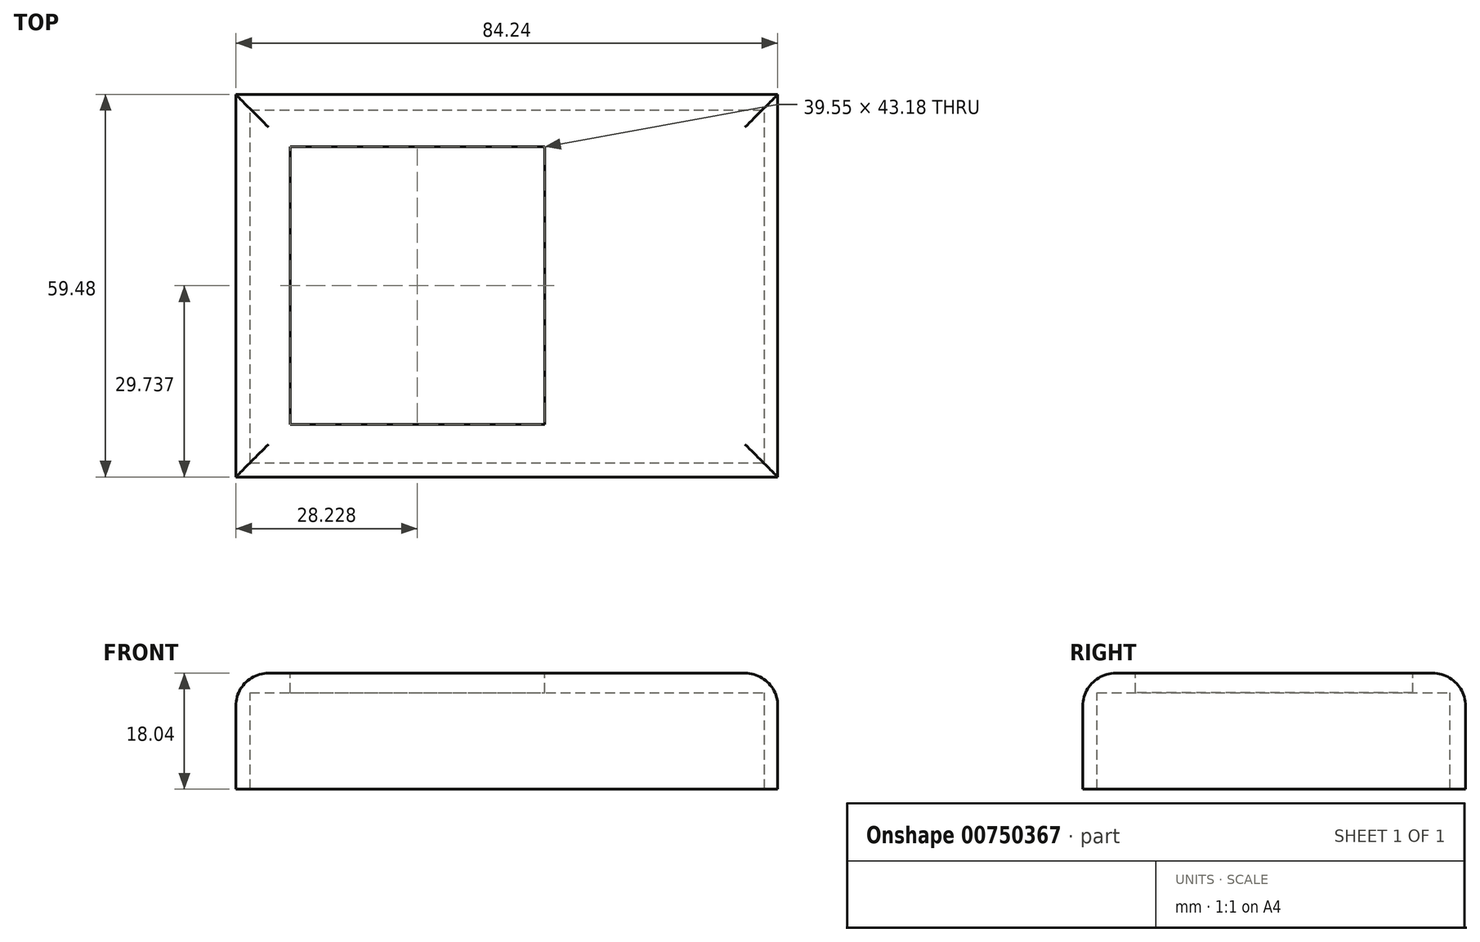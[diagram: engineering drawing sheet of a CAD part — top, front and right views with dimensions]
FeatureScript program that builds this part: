
annotation { "Feature Type Name" : "Feature", "Feature Type Description" : "" }
export const myFeature = defineFeature(function(context is Context, id is Id, definition is map)
    precondition{}
    {
        {
            var Q0;
            Q0=qCreatedBy(makeId("Top.planeOp"),FACE);
            var sketch = newSketch(context, id + "F0", { "sketchPlane" : qUnion([Q0])});
            skLineSegment(sketch, "E0.bottom", {"start": v(-43.4, 26.95) * mm, "end": v(40.84, 26.95) * mm});
            skLineSegment(sketch, "E0.top", {"start": v(-43.4, -32.53) * mm, "end": v(40.84, -32.53) * mm});
            skLineSegment(sketch, "E0.left", {"start": v(-43.4, 26.95) * mm, "end": v(-43.4, -32.53) * mm});
            skLineSegment(sketch, "E0.right", {"start": v(40.84, 26.95) * mm, "end": v(40.84, -32.53) * mm});
            skSolve(sketch);
        }
        {
            var Q0;
            Q0 = qSketchRegion(id + "F0", true);
            extrude(context, id + "F1", {"entities" : qUnion([Q0]), "depth" : 3.05 * mm, "offsetDistance" : 25.4 * mm});
        }
        {
            var Q0;
            Q0=makeQuery(id+"F1.opExtrude","CAP_FACE",FACE,{"disambiguationData":[OSD([sQuery(id+"F0.wireOp",EDGE,"E0.bottom"),sQuery(id+"F0.wireOp",EDGE,"E0.top"),sQuery(id+"F0.wireOp",EDGE,"E0.left"),sQuery(id+"F0.wireOp",EDGE,"E0.right")])],"isStart":true});
            var sketch = newSketch(context, id + "F2", { "sketchPlane" : qUnion([Q0])});
            skLineSegment(sketch, "E1.bottom", {"start": v(-41.19, 30.32) * mm, "end": v(38.81, 30.32) * mm});
            skLineSegment(sketch, "E1.top", {"start": v(-41.19, -24.56) * mm, "end": v(38.81, -24.56) * mm});
            skLineSegment(sketch, "E1.left", {"start": v(-41.19, 30.32) * mm, "end": v(-41.19, -24.56) * mm});
            skLineSegment(sketch, "E1.right", {"start": v(38.81, 30.32) * mm, "end": v(38.81, -24.56) * mm});
            skLineSegment(sketch, "E2.bottom", {"start": v(-43.4, 32.53) * mm, "end": v(40.84, 32.53) * mm});
            skLineSegment(sketch, "E2.top", {"start": v(-43.4, -26.95) * mm, "end": v(40.84, -26.95) * mm});
            skLineSegment(sketch, "E2.left", {"start": v(-43.4, 32.53) * mm, "end": v(-43.4, -26.95) * mm});
            skLineSegment(sketch, "E2.right", {"start": v(40.84, 32.53) * mm, "end": v(40.84, -26.95) * mm});
            skSolve(sketch);
        }
        {
            var Q0;
            Q0 = qSketchRegion(id + "F2", true);
            extrude(context, id + "F3", {"entities" : qUnion([Q0]), "operationType" : NewBodyOperationType.ADD, "depth" : 15 * mm, "offsetDistance" : 25.4 * mm});
        }
        {
            var Q0;
            Q0=makeQuery(id+"F1.opExtrude","CAP_EDGE",EDGE,{"disambiguationData":[OSD([sQuery(id+"F0.wireOp",EDGE,"E0.left")])],"isStart":false});
            var Q1;
            Q1=makeQuery(id+"F1.opExtrude","CAP_EDGE",EDGE,{"disambiguationData":[OSD([sQuery(id+"F0.wireOp",EDGE,"E0.top")])],"isStart":false});
            var Q2;
            Q2=makeQuery(id+"F1.opExtrude","CAP_EDGE",EDGE,{"disambiguationData":[OSD([sQuery(id+"F0.wireOp",EDGE,"E0.right")])],"isStart":false});
            var Q3;
            Q3=makeQuery(id+"F1.opExtrude","CAP_EDGE",EDGE,{"disambiguationData":[OSD([sQuery(id+"F0.wireOp",EDGE,"E0.bottom")])],"isStart":false});
            fillet(context, id + "F4", {"entities" : qUnion([Q0, Q1, Q2, Q3]), "radius" : 5.08 * mm, "tangentPropagation" : true, "allowEdgeOverflow" : false});
        }
        {
            var Q0;
            Q0=makeQuery(id+"F1.opExtrude","CAP_FACE",FACE,{"disambiguationData":[OSD([sQuery(id+"F0.wireOp",EDGE,"E0.bottom"),sQuery(id+"F0.wireOp",EDGE,"E0.top"),sQuery(id+"F0.wireOp",EDGE,"E0.left"),sQuery(id+"F0.wireOp",EDGE,"E0.right")])],"isStart":false});
            var sketch = newSketch(context, id + "F5", { "sketchPlane" : qUnion([Q0])});
            skLineSegment(sketch, "E3.bottom", {"start": v(-34.95, 18.8) * mm, "end": v(4.6, 18.8) * mm});
            skLineSegment(sketch, "E3.top", {"start": v(-34.95, -24.38) * mm, "end": v(4.6, -24.38) * mm});
            skLineSegment(sketch, "E3.left", {"start": v(-34.95, 18.8) * mm, "end": v(-34.95, -24.38) * mm});
            skLineSegment(sketch, "E3.right", {"start": v(4.6, 18.8) * mm, "end": v(4.6, -24.38) * mm});
            skSolve(sketch);
        }
        {
            var Q0;
            Q0 = qSketchRegion(id + "F5", true);
            extrude(context, id + "F6", {"entities" : qUnion([Q0]), "operationType" : NewBodyOperationType.REMOVE, "oppositeDirection" : true, "depth" : 25.4 * mm, "offsetDistance" : 25.4 * mm});
        }
    });
